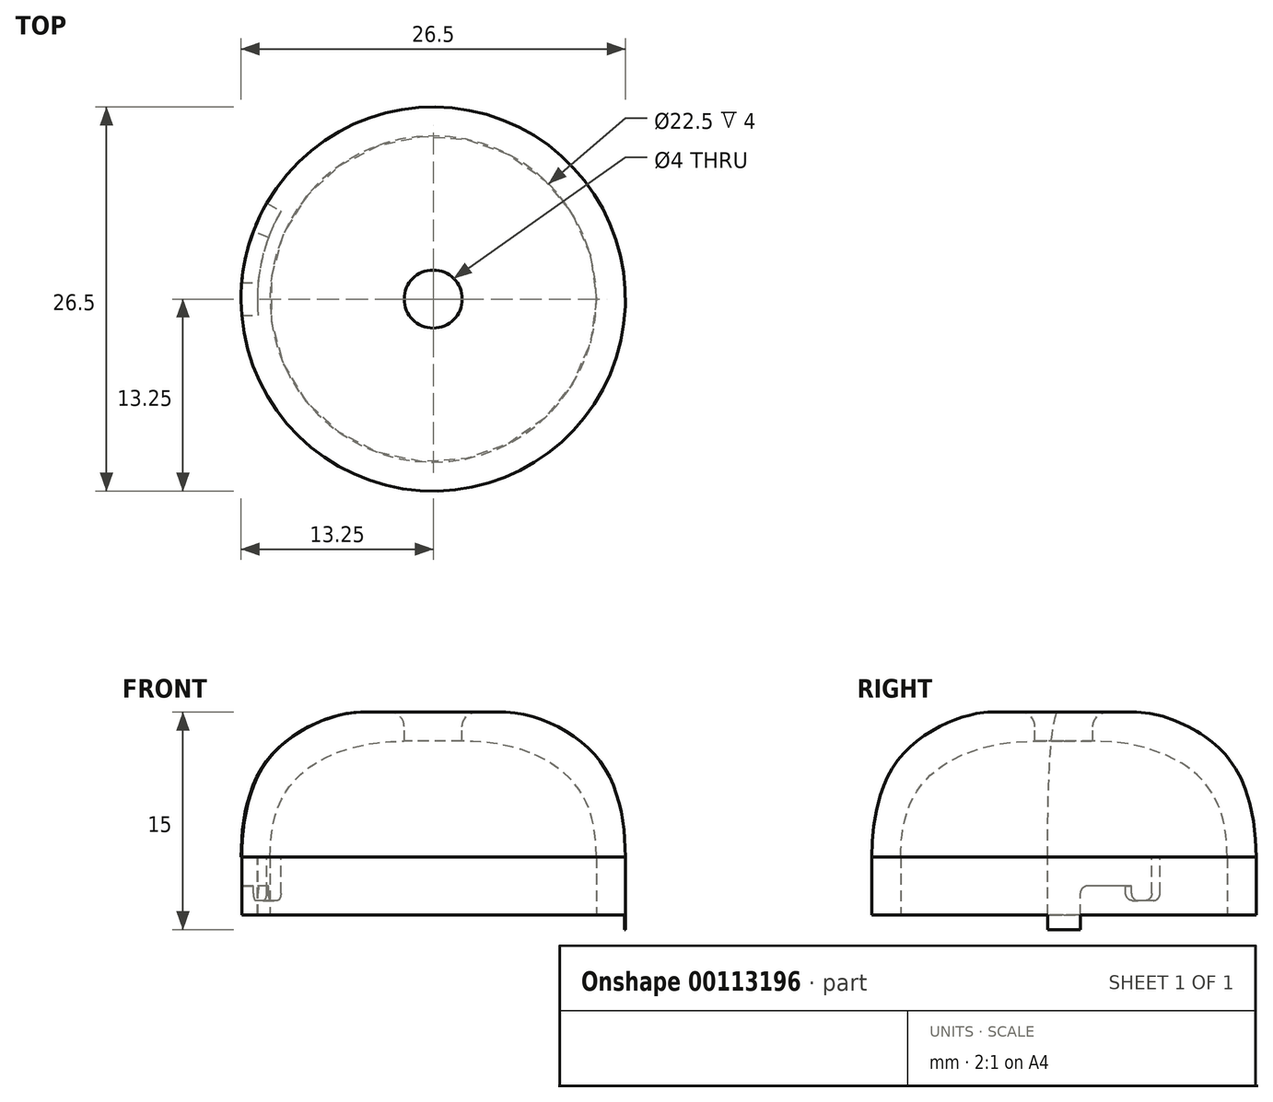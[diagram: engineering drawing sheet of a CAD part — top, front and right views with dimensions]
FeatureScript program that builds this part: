
annotation { "Feature Type Name" : "Feature", "Feature Type Description" : "" }
export const myFeature = defineFeature(function(context is Context, id is Id, definition is map)
    precondition{}
    {
        {
            var Q0;
            Q0=qCreatedBy(makeId("Top.planeOp"),FACE);
            var sketch = newSketch(context, id + "F0", { "sketchPlane" : qUnion([Q0])});
            skCircle(sketch, "E0", {"center": v(0, 0) * mm, "radius": 13.25 * mm});
            skCircle(sketch, "E1.0", {"center": v(0, 0) * mm, "radius": 11.25 * mm});
            skSolve(sketch);
        }
        {
            var Q0;
            Q0=makeQuery(id+"F0.imprint","IMPRINT",FACE,{"disambiguationData":[TD([[makeQuery(id+"F0.imprint","IMPRINT",EDGE,{"derivedFrom":sQuery(id+"F0.wireOp",EDGE,"E0")}),1.0]])]});
            extrude(context, id + "F1", {"entities" : qUnion([Q0]), "depth" : 5 * mm});
        }
        {
            var Q0;
            Q0=makeQuery(id+"F1.opExtrude","CAP_FACE",FACE,{"disambiguationData":[OSD([sQuery(id+"F0.wireOp",EDGE,"E0"),sQuery(id+"F0.wireOp",EDGE,"E1.0")])],"isStart":false});
            var sketch = newSketch(context, id + "F2", { "sketchPlane" : qUnion([Q0])});
            skLineSegment(sketch, "E2.bottom", {"start": v(-13.2, 1.13) * mm, "end": v(-12.07, 1.13) * mm});
            skLineSegment(sketch, "E2.top", {"start": v(-13.2, -1.13) * mm, "end": v(-12.07, -1.13) * mm});
            skLineSegment(sketch, "E2.left", {"start": v(-13.2, 1.13) * mm, "end": v(-13.2, -1.13) * mm, "construction": true});
            skLineSegment(sketch, "E2.right", {"start": v(13.2, 1.13) * mm, "end": v(13.2, -1.13) * mm, "construction": true});
            skPoint(sketch, "E2.middle", {"position": v(0, 0) * mm});
            skLineSegment(sketch, "E3", {"start": v(-11.47, 6.62) * mm, "end": v(-10.5, 6.06) * mm});
            skArc(sketch, "E4", {"start": v(-11.47, 6.62) * mm, "mid": v(-12.64, 3.97) * mm, "end": v(-13.2, 1.12) * mm});
            skArc(sketch, "E5", {"start": v(13.2, 1.12) * mm, "mid": v(2.88, 12.93) * mm, "end": v(-11.47, 6.62) * mm, "construction": true});
            skArc(sketch, "E6", {"start": v(13.2, -1.12) * mm, "mid": v(13.25, 0) * mm, "end": v(13.2, 1.12) * mm});
            skArc(sketch, "E7", {"start": v(11.47, -6.62) * mm, "mid": v(12.64, -3.97) * mm, "end": v(13.2, -1.12) * mm});
            skArc(sketch, "E8", {"start": v(-13.2, -1.12) * mm, "mid": v(-2.88, -12.93) * mm, "end": v(11.47, -6.62) * mm, "construction": true});
            skArc(sketch, "E9", {"start": v(-13.2, 1.12) * mm, "mid": v(-13.25, 0) * mm, "end": v(-13.2, -1.12) * mm});
            skArc(sketch, "E10", {"start": v(-11.2, -1.13) * mm, "mid": v(-2.36, -11) * mm, "end": v(9.74, -5.62) * mm, "construction": true});
            skArc(sketch, "E11", {"start": v(-11.2, 1.12) * mm, "mid": v(-11.25, 0) * mm, "end": v(-11.2, -1.13) * mm, "construction": true});
            skArc(sketch, "E12", {"start": v(-9.74, 5.62) * mm, "mid": v(-10.7, 3.45) * mm, "end": v(-11.2, 1.12) * mm, "construction": true});
            skArc(sketch, "E13", {"start": v(11.2, 1.13) * mm, "mid": v(2.36, 11) * mm, "end": v(-9.74, 5.62) * mm, "construction": true});
            skArc(sketch, "E14", {"start": v(11.2, -1.12) * mm, "mid": v(11.25, 0) * mm, "end": v(11.2, 1.12) * mm});
            skArc(sketch, "E15", {"start": v(9.74, -5.62) * mm, "mid": v(10.7, -3.45) * mm, "end": v(11.2, -1.12) * mm});
            skLineSegment(sketch, "E16", {"start": v(11.2, -1.13) * mm, "end": v(13.2, -1.13) * mm});
            skLineSegment(sketch, "E17", {"start": v(11.2, 1.13) * mm, "end": v(13.2, 1.13) * mm});
            skLineSegment(sketch, "E18", {"start": v(-11.2, 1.13) * mm, "end": v(11.2, 1.13) * mm, "construction": true});
            skLineSegment(sketch, "E19", {"start": v(-11.2, -1.13) * mm, "end": v(11.2, -1.13) * mm, "construction": true});
            skLineSegment(sketch, "E20", {"start": v(-9.74, 5.62) * mm, "end": v(9.74, -5.62) * mm, "construction": true});
            skLineSegment(sketch, "E21", {"start": v(9.74, -5.62) * mm, "end": v(11.47, -6.63) * mm});
            skArc(sketch, "E22.0", {"start": v(-10.5, 6.06) * mm, "mid": v(-11.84, 2.6) * mm, "end": v(-12.07, -1.13) * mm});
            skArc(sketch, "E23.0", {"start": v(12.32, -1.12) * mm, "mid": v(12.38, 0) * mm, "end": v(12.32, 1.13) * mm});
            skLineSegment(sketch, "E24", {"start": v(-10.5, 6.06) * mm, "end": v(-9.74, 5.62) * mm, "construction": true});
            skLineSegment(sketch, "E25", {"start": v(-12.07, 1.13) * mm, "end": v(-11.2, 1.13) * mm, "construction": true});
            skLineSegment(sketch, "E26", {"start": v(-12.07, -1.13) * mm, "end": v(-11.2, -1.13) * mm, "construction": true});
            skSolve(sketch);
        }
        {
            var Q0;
            {var subQ0=sQuery(id+"F2.wireOp",EDGE,"E2.bottom");Q0=makeQuery(id+"F2.imprint","IMPRINT",FACE,{"disambiguationData":[TD([[makeQuery(id+"F2.imprint","IMPRINT",EDGE,{"derivedFrom":subQ0}),-1.0]])]});}
            var Q1;
            {var subQ0=sQuery(id+"F2.wireOp",EDGE,"E2.bottom");Q1=makeQuery(id+"F2.imprint","IMPRINT",FACE,{"disambiguationData":[TD([[makeQuery(id+"F2.imprint","IMPRINT",EDGE,{"derivedFrom":subQ0}),1.0]])]});}
            extrude(context, id + "F3", {"entities" : qUnion([Q0, Q1]), "operationType" : NewBodyOperationType.REMOVE, "oppositeDirection" : true, "depth" : 2 * mm});
        }
        {
            var Q0;
            {var subQ0=sQuery(id+"F2.wireOp",EDGE,"E2.bottom");Q0=makeQuery(id+"F2.imprint","IMPRINT",FACE,{"disambiguationData":[TD([[makeQuery(id+"F2.imprint","IMPRINT",EDGE,{"derivedFrom":subQ0}),-1.0]])]});}
            extrude(context, id + "F4", {"entities" : qUnion([Q0]), "operationType" : NewBodyOperationType.REMOVE, "oppositeDirection" : true, "depth" : 25 * mm});
        }
        {
            var Q0;
            Q0=qCreatedBy(makeId("Front.planeOp"),FACE);
            var sketch = newSketch(context, id + "F5", { "sketchPlane" : qUnion([Q0])});
            skLineSegment(sketch, "E27", {"start": v(0, 9.92) * mm, "end": v(0, 0) * mm});
            skSolve(sketch);
        }
        {
            var Q0;
            Q0=makeQuery(id+"F3.boolean.opBoolean","COPY",FACE,{"derivedFrom":makeQuery(id+"F3.opExtrude","CAP_FACE",FACE,{"disambiguationData":[OSD([sQuery(id+"F2.wireOp",EDGE,"E2.top"),sQuery(id+"F2.wireOp",EDGE,"E3"),sQuery(id+"F2.wireOp",EDGE,"E4"),sQuery(id+"F2.wireOp",EDGE,"E9"),sQuery(id+"F2.wireOp",EDGE,"E22.0")])],"isStart":false})});
            var sketch = newSketch(context, id + "F6", { "sketchPlane" : qUnion([Q0])});
            skLineSegment(sketch, "E28", {"start": v(0, 0) * mm, "end": v(-11.35, 4.25) * mm, "construction": true});
            skArc(sketch, "E29.0", {"start": v(-11.47, 6.62) * mm, "mid": v(-11.98, 5.66) * mm, "end": v(-12.4, 4.65) * mm});
            skArc(sketch, "E29.1", {"start": v(-10.5, 6.06) * mm, "mid": v(-10.96, 5.18) * mm, "end": v(-11.35, 4.25) * mm});
            skLineSegment(sketch, "E29.2", {"start": v(-11.47, 6.62) * mm, "end": v(-10.5, 6.06) * mm});
            skPoint(sketch, "E30.orphan", {"position": v(-12.07, -1.13) * mm});
            skPoint(sketch, "E31.orphan", {"position": v(-13.2, 1.12) * mm});
            skLineSegment(sketch, "E32", {"start": v(-11.35, 4.25) * mm, "end": v(-12.4, 4.65) * mm});
            skSolve(sketch);
        }
        {
            var Q0;
            Q0=makeQuery(id+"F6.imprint","IMPRINT",FACE,{"disambiguationData":[TD([[makeQuery(id+"F6.imprint","IMPRINT",EDGE,{"derivedFrom":sQuery(id+"F6.wireOp",EDGE,"E29.0")}),1.0]])]});
            extrude(context, id + "F7", {"entities" : qUnion([Q0]), "operationType" : NewBodyOperationType.REMOVE, "oppositeDirection" : true, "depth" : 1 * mm});
        }
        {
            var Q0;
            Q0=makeQuery(id+"F7.boolean.opBoolean","COPY",EDGE,{"derivedFrom":makeQuery(id+"F7.opExtrude","CAP_EDGE",EDGE,{"disambiguationData":[OSD([sQuery(id+"F6.wireOp",EDGE,"E32")])],"isStart":true})});
            var Q1;
            Q1=makeQuery(id+"F4.boolean.opBoolean","INTERSECT",EDGE,{"derivedFrom":[makeQuery(id+"F3.boolean.opBoolean","COPY",FACE,{"derivedFrom":makeQuery(id+"F3.opExtrude","CAP_FACE",FACE,{"disambiguationData":[OSD([sQuery(id+"F2.wireOp",EDGE,"E2.top"),sQuery(id+"F2.wireOp",EDGE,"E3"),sQuery(id+"F2.wireOp",EDGE,"E4"),sQuery(id+"F2.wireOp",EDGE,"E9"),sQuery(id+"F2.wireOp",EDGE,"E22.0")])],"isStart":false})}),makeQuery(id+"F4.opExtrude","SWEPT_FACE",FACE,{"disambiguationData":[OSD([sQuery(id+"F2.wireOp",EDGE,"E2.bottom")])]})]});
            var Q2;
            Q2=makeQuery(id+"F7.boolean.opBoolean","COPY",EDGE,{"derivedFrom":makeQuery(id+"F7.opExtrude","CAP_EDGE",EDGE,{"disambiguationData":[OSD([sQuery(id+"F6.wireOp",EDGE,"E29.2")])],"isStart":false})});
            var Q3;
            Q3=makeQuery(id+"F7.boolean.opBoolean","COPY",EDGE,{"derivedFrom":makeQuery(id+"F7.opExtrude","CAP_EDGE",EDGE,{"disambiguationData":[OSD([sQuery(id+"F6.wireOp",EDGE,"E32")])],"isStart":false})});
            fillet(context, id + "F8", {"entities" : qUnion([Q0, Q1, Q2, Q3]), "radius" : .5 * mm, "tangentPropagation" : true, "allowEdgeOverflow" : false});
        }
        {
            var Q0;
            Q0=makeQuery(id+"F1.opExtrude","CAP_FACE",FACE,{"disambiguationData":[OSD([sQuery(id+"F0.wireOp",EDGE,"E0"),sQuery(id+"F0.wireOp",EDGE,"E1.0")])],"isStart":false});
            var sketch = newSketch(context, id + "F9", { "sketchPlane" : qUnion([Q0])});
            skCircle(sketch, "E33", {"center": v(0, 0) * mm, "radius": 13.25 * mm});
            skSolve(sketch);
        }
        {
            var Q0;
            Q0=makeQuery(id+"F9.imprint","IMPRINT",FACE,{"disambiguationData":[TD([[makeQuery(id+"F9.imprint","IMPRINT",EDGE,{"derivedFrom":makeQuery(id+"F1.opExtrude","CAP_EDGE",EDGE,{"disambiguationData":[OSD([sQuery(id+"F0.wireOp",EDGE,"E1.0")])],"isStart":false})}),-1.0]])]});
            cPlane(context, id + "F10", {"entities" : qUnion([Q0]), "cplaneType" : CPlaneType.OFFSET, "offset" : 10 * mm, "width" : 150 * mm, "height" : 150 * mm});
        }
        {
            var Q0;
            Q0=qCreatedBy(id+"F10.planeOp",FACE);
            var sketch = newSketch(context, id + "F11", { "sketchPlane" : qUnion([Q0])});
            skCircle(sketch, "E34", {"center": v(0, 0) * mm, "radius": 5 * mm});
            skCircle(sketch, "E35.0", {"center": v(0, 0) * mm, "radius": 2 * mm});
            skSolve(sketch);
        }
        {
            var Q0;
            Q0=qCreatedBy(makeId("Front.planeOp"),FACE);
            var sketch = newSketch(context, id + "F12", { "sketchPlane" : qUnion([Q0])});
            skFitSpline(sketch, "E36", {"points": [v(-13.25, 5) * mm, v(-11.18, 12.02) * mm, v(-5, 15) * mm], "startDerivative": vector(0, 13.06) * mm, "endDerivative": vector(10.36, 0) * mm});
            skFitSpline(sketch, "E37", {"points": [v(-11.25, 5) * mm, v(-9, 10.83) * mm, v(-2, 13) * mm], "startDerivative": vector(0, 17.72) * mm, "endDerivative": vector(17.32, 0) * mm});
            skLineSegment(sketch, "E38", {"start": v(-5, 15) * mm, "end": v(-2, 15) * mm});
            skLineSegment(sketch, "E39", {"start": v(-2, 15) * mm, "end": v(-2, 13) * mm});
            skLineSegment(sketch, "E40", {"start": v(-2, 13) * mm, "end": v(0.65, 13) * mm, "construction": true});
            skLineSegment(sketch, "E41", {"start": v(-11.25, 5) * mm, "end": v(-13.25, 5) * mm});
            skLineSegment(sketch, "E42", {"start": v(-13.25, 9.45) * mm, "end": v(-13.25, 5) * mm, "construction": true});
            skLineSegment(sketch, "E43", {"start": v(-11.25, 8.43) * mm, "end": v(-11.25, 5) * mm, "construction": true});
            skSolve(sketch);
        }
        {
            var Q0;
            Q0=makeQuery(id+"F12.imprint","IMPRINT",FACE,{"disambiguationData":[TD([[makeQuery(id+"F12.imprint","IMPRINT",EDGE,{"derivedFrom":sQuery(id+"F12.wireOp",EDGE,"E36")}),-1.0]])]});
            var Q1;
            Q1=sQuery(id+"F5.wireOp",EDGE,"E27");
            revolve(context, id + "F13", {"operationType" : NewBodyOperationType.ADD, "entities" : qUnion([Q0]), "axis" : qUnion([Q1]), "revolveType" : RevolveType.FULL});
        }
        {
            var Q0;
            Q0=qCreatedBy(makeId("Front.planeOp"),FACE);
            var sketch = newSketch(context, id + "F14", { "sketchPlane" : qUnion([Q0])});
            skLineSegment(sketch, "E44.bottom", {"start": v(-13.2, 0) * mm, "end": v(13.2, 0) * mm});
            skLineSegment(sketch, "E44.top", {"start": v(-13.2, 1) * mm, "end": v(13.2, 1) * mm});
            skLineSegment(sketch, "E44.left", {"start": v(-13.2, 0) * mm, "end": v(-13.2, 1) * mm});
            skLineSegment(sketch, "E44.right", {"start": v(13.2, 0) * mm, "end": v(13.2, 1) * mm});
            skSolve(sketch);
        }
        {
            var Q0;
            Q0=makeQuery(id+"F14.imprint","IMPRINT",FACE,{"disambiguationData":[TD([[makeQuery(id+"F14.imprint","IMPRINT",EDGE,{"derivedFrom":sQuery(id+"F14.wireOp",EDGE,"E44.bottom")}),1.0]])]});
            extrude(context, id + "F15", {"entities" : qUnion([Q0]), "operationType" : NewBodyOperationType.REMOVE, "endBound" : BoundingType.THROUGH_ALL, "oppositeDirection" : true, "depth" : 25 * mm, "hasSecondDirection" : true, "secondDirectionBound" : SecondDirectionBoundingType.THROUGH_ALL, "secondDirectionOppositeDirection" : false, "secondDirectionDepth" : 25 * mm});
        }
        {
            var Q0;
            Q0=makeQuery(id+"F13.opRevolve","SWEPT_EDGE",EDGE,{"disambiguationData":[OSD([sQuery(id+"F12.wireOp",EDGE,"E38"),sQuery(id+"F12.wireOp",EDGE,"E39")])]});
            fillet(context, id + "F16", {"entities" : qUnion([Q0]), "radius" : 1 * mm, "tangentPropagation" : true, "allowEdgeOverflow" : false});
        }
    });
